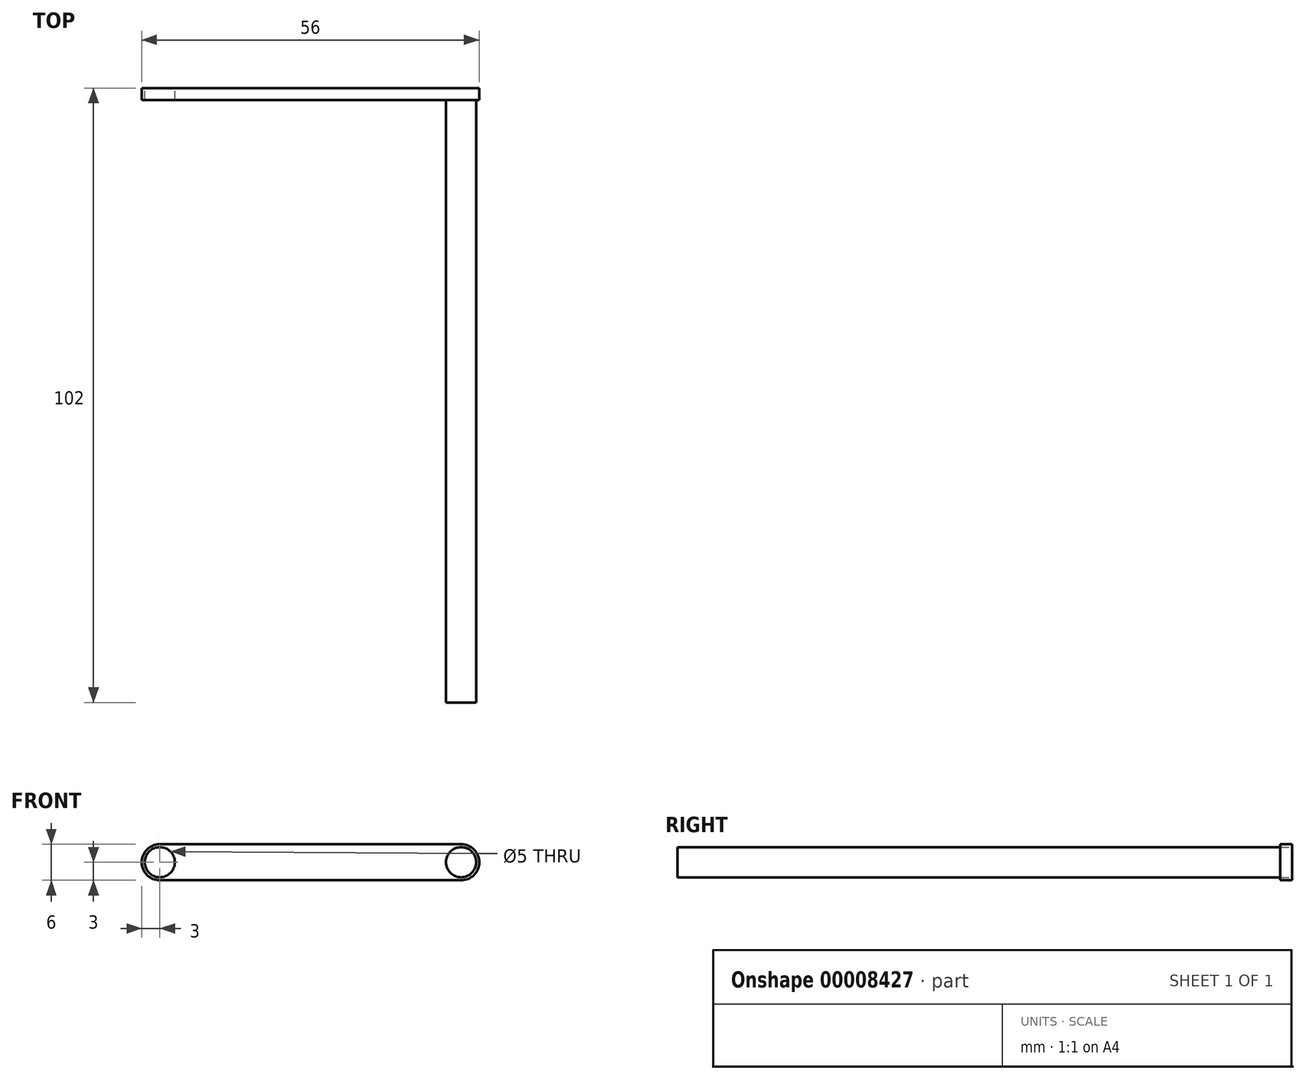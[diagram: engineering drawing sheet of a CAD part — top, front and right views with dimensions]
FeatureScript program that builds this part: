
annotation { "Feature Type Name" : "Feature", "Feature Type Description" : "" }
export const myFeature = defineFeature(function(context is Context, id is Id, definition is map)
    precondition{}
    {
        {
            var Q0;
            Q0=qCreatedBy(makeId("Front.planeOp"),FACE);
            var sketch = newSketch(context, id + "F0", { "sketchPlane" : qUnion([Q0])});
            skLineSegment(sketch, "E0.bottom", {"start": v(0, 0) * mm, "end": v(50, 0) * mm});
            skLineSegment(sketch, "E0.top", {"start": v(0, -6) * mm, "end": v(50, -6) * mm});
            skLineSegment(sketch, "E0.left", {"start": v(0, 0) * mm, "end": v(0, -6) * mm});
            skLineSegment(sketch, "E0.right", {"start": v(50, 0) * mm, "end": v(50, -6) * mm});
            skArc(sketch, "E1", {"start": v(0, 0) * mm, "mid": v(-3, -3) * mm, "end": v(0, -6) * mm});
            skArc(sketch, "E2", {"start": v(50, -6) * mm, "mid": v(53, -3) * mm, "end": v(50, 0) * mm});
            skCircle(sketch, "E3", {"center": v(0, -3) * mm, "radius": 2.5 * mm});
            skSolve(sketch);
        }
        {
            var Q0;
            Q0 = qSketchRegion(id + "F0", true);
            extrude(context, id + "F1", {"entities" : qUnion([Q0]), "depth" : 2 * mm});
        }
        {
            var Q0;
            Q0=makeQuery(id+"F1.opExtrude","CAP_FACE",FACE,{"disambiguationData":[OSD([sQuery(id+"F0.wireOp",EDGE,"E0.bottom"),sQuery(id+"F0.wireOp",EDGE,"E0.top"),sQuery(id+"F0.wireOp",EDGE,"E1"),sQuery(id+"F0.wireOp",EDGE,"E2"),sQuery(id+"F0.wireOp",EDGE,"E3")])],"isStart":false});
            var sketch = newSketch(context, id + "F2", { "sketchPlane" : qUnion([Q0])});
            skCircle(sketch, "E4", {"center": v(50, -3) * mm, "radius": 2.5 * mm});
            skSolve(sketch);
        }
        {
            var Q0;
            Q0 = qSketchRegion(id + "F2", true);
            extrude(context, id + "F3", {"entities" : qUnion([Q0]), "operationType" : NewBodyOperationType.ADD, "depth" : 100 * mm});
        }
    });
